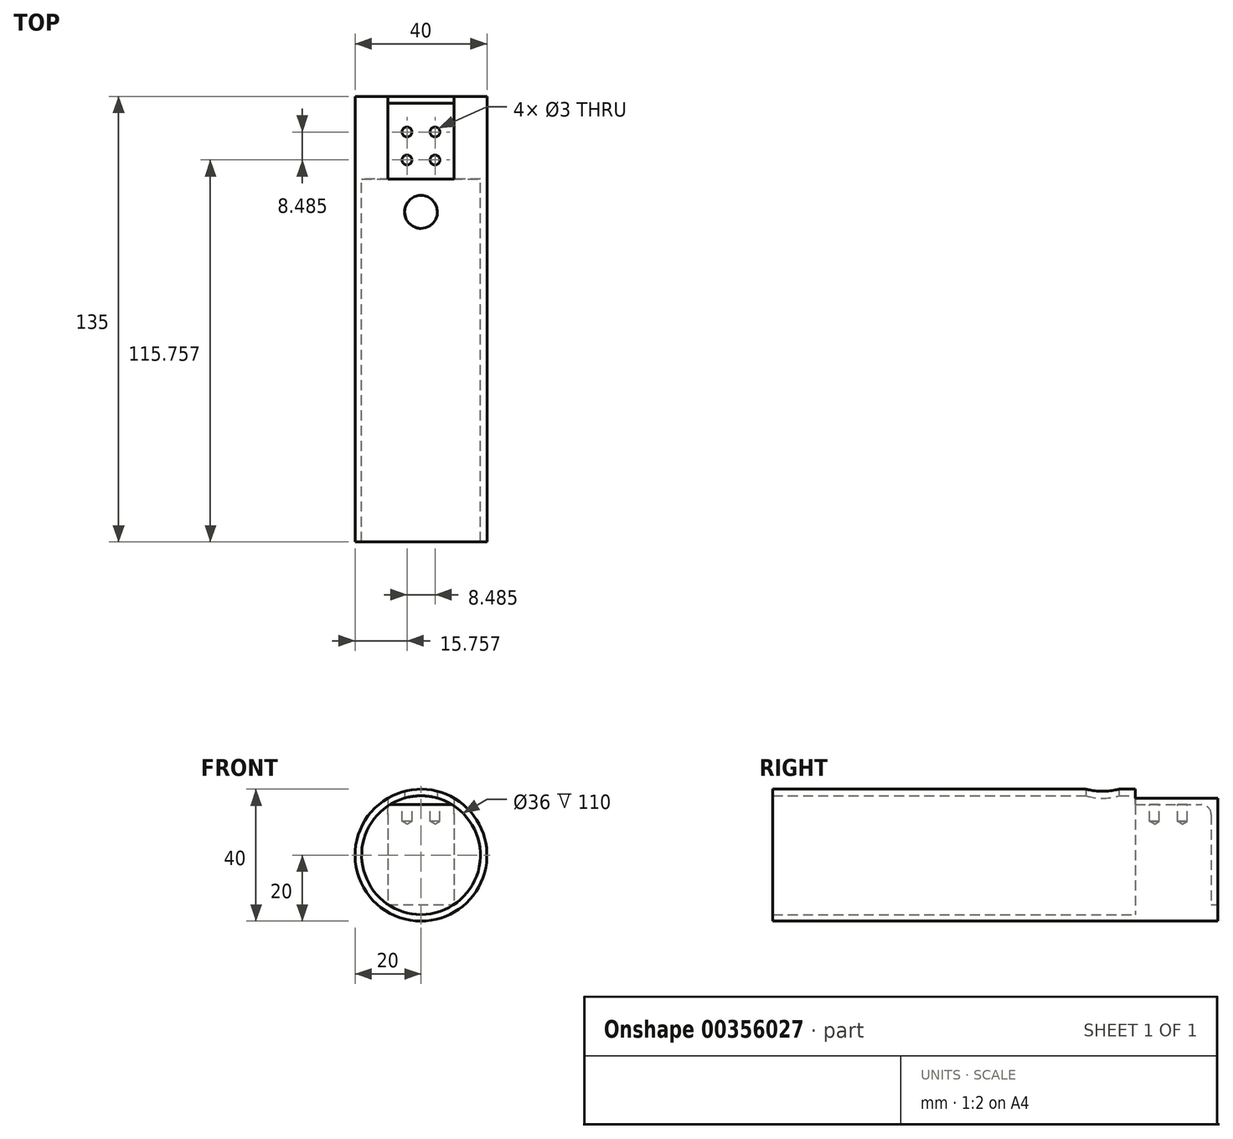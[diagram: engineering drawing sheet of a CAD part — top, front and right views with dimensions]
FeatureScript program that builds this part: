
annotation { "Feature Type Name" : "Feature", "Feature Type Description" : "" }
export const myFeature = defineFeature(function(context is Context, id is Id, definition is map)
    precondition{}
    {
        {
            var Q0;
            Q0=qCreatedBy(makeId("Front.planeOp"),FACE);
            var sketch = newSketch(context, id + "F0", { "sketchPlane" : qUnion([Q0])});
            skCircle(sketch, "E0", {"center": v(0, 0) * mm, "radius": 13.5 * mm});
            skCircle(sketch, "E1", {"center": v(0, 0) * mm, "radius": 20 * mm});
            skLineSegment(sketch, "E2.top", {"start": v(10, 15.32) * mm, "end": v(-10, 15.32) * mm});
            skLineSegment(sketch, "E2.left", {"start": v(10, 17.32) * mm, "end": v(10, 15.32) * mm});
            skLineSegment(sketch, "E2.right", {"start": v(-10, 17.32) * mm, "end": v(-10, 15.32) * mm});
            skPoint(sketch, "E3", {"position": v(10, 17.32) * mm});
            skCircle(sketch, "E4", {"center": v(0, 0) * mm, "radius": 18 * mm});
            skSolve(sketch);
        }
        {
            var Q0;
            {var subQ0=sQuery(id+"F0.wireOp",EDGE,"E2.left");Q0=makeQuery(id+"F0.imprint","IMPRINT",FACE,{"disambiguationData":[TD([[makeQuery(id+"F0.imprint","IMPRINT",EDGE,{"derivedFrom":subQ0}),1.0]])]});}
            extrude(context, id + "F1", {"entities" : qUnion([Q0]), "depth" : 135 * mm});
        }
        {
            var Q0;
            Q0=makeQuery(id+"F0.imprint","IMPRINT",FACE,{"disambiguationData":[TD([[makeQuery(id+"F0.imprint","IMPRINT",EDGE,{"derivedFrom":sQuery(id+"F0.wireOp",EDGE,"E2.top")}),-1.0]])]});
            extrude(context, id + "F2", {"entities" : qUnion([Q0]), "operationType" : NewBodyOperationType.ADD, "depth" : 135 * mm, "hasSecondDirection" : true, "secondDirectionOppositeDirection" : true, "secondDirectionDepth" : -25 * mm});
        }
        {
            var Q0;
            Q0=makeQuery(id+"F0.imprint","IMPRINT",FACE,{"disambiguationData":[TD([[makeQuery(id+"F0.imprint","IMPRINT",EDGE,{"derivedFrom":sQuery(id+"F0.wireOp",EDGE,"E0")}),1.0]])]});
            var Q1;
            Q1=makeQuery(id+"F0.imprint","IMPRINT",FACE,{"disambiguationData":[TD([[makeQuery(id+"F0.imprint","IMPRINT",EDGE,{"derivedFrom":sQuery(id+"F0.wireOp",EDGE,"E0")}),-1.0]])]});
            extrude(context, id + "F3", {"entities" : qUnion([Q0, Q1]), "operationType" : NewBodyOperationType.ADD, "depth" : 25 * mm});
        }
        {
            var Q0;
            Q0=qCreatedBy(makeId("Front.planeOp"),FACE);
            var sketch = newSketch(context, id + "F4", { "sketchPlane" : qUnion([Q0])});
            skLineSegment(sketch, "E5.bottom", {"start": v(-10, 21.25) * mm, "end": v(10, 21.25) * mm});
            skLineSegment(sketch, "E5.top", {"start": v(-10, -15) * mm, "end": v(10, -15) * mm});
            skLineSegment(sketch, "E5.left", {"start": v(-10, 21.25) * mm, "end": v(-10, -15) * mm});
            skLineSegment(sketch, "E5.right", {"start": v(10, 21.25) * mm, "end": v(10, -15) * mm});
            skSolve(sketch);
        }
        {
            var Q0;
            Q0 = qSketchRegion(id + "F4", true);
            extrude(context, id + "F5", {"entities" : qUnion([Q0]), "operationType" : NewBodyOperationType.REMOVE, "oppositeDirection" : true, "depth" : -2 * mm});
        }
        {
            var Q0;
            {var subQ0=sQuery(id+"F0.wireOp",EDGE,"E2.top");Q0=makeQuery(id+"F3.boolean.opBoolean","MERGE",FACE,{"derivedFrom":[makeQuery(id+"F1.opExtrude","SWEPT_FACE",FACE,{"disambiguationData":[OSD([subQ0]),TDD([makeQuery(id+"F0.imprint","IMPRINT",EDGE,{"disambiguationData":[TD([[makeQuery(id+"F0.imprint","INTERSECT",VERTEX,{"derivedFrom":[subQ0,sQuery(id+"F0.wireOp",EDGE,"E2.left")]}),-1.0]])],"derivedFrom":subQ0})])]}),makeQuery(id+"F1.opExtrude","SWEPT_FACE",FACE,{"disambiguationData":[OSD([subQ0]),TDD([makeQuery(id+"F0.imprint","IMPRINT",EDGE,{"disambiguationData":[TD([[makeQuery(id+"F0.imprint","INTERSECT",VERTEX,{"derivedFrom":[subQ0,sQuery(id+"F0.wireOp",EDGE,"E2.right")]}),1.0]])],"derivedFrom":subQ0})])]}),makeQuery(id+"F3.opExtrude","SWEPT_FACE",FACE,{"disambiguationData":[OSD([subQ0])]})]});}
            var sketch = newSketch(context, id + "F6", { "sketchPlane" : qUnion([Q0])});
            skPoint(sketch, "E6", {"position": v(0, -15) * mm});
            skPoint(sketch, "E7", {"position": v(0, -9) * mm});
            skPoint(sketch, "E8.1.0", {"position": v(-4.24, -10.76) * mm});
            skPoint(sketch, "E8.3.0", {"position": v(-4.24, -19.24) * mm});
            skPoint(sketch, "E8.5.0", {"position": v(4.24, -19.24) * mm});
            skPoint(sketch, "E8.7.0", {"position": v(4.24, -10.76) * mm});
            skSolve(sketch);
        }
        {
            var Q0;
            Q0=sQuery(id+"F6.wireOp",VERTEX,"E8.7.0");
            var Q1;
            Q1=sQuery(id+"F6.wireOp",VERTEX,"E8.1.0");
            var Q2;
            Q2=sQuery(id+"F6.wireOp",VERTEX,"E8.3.0");
            var Q3;
            Q3=sQuery(id+"F6.wireOp",VERTEX,"E8.5.0");
            var Q4;
            Q4=makeQuery(id+"F1.opExtrude","SWEPT_BODY",BODY,{"disambiguationData":[OSD([sQuery(id+"F0.wireOp",EDGE,"E1"),sQuery(id+"F0.wireOp",EDGE,"E2.top"),sQuery(id+"F0.wireOp",EDGE,"E2.left"),sQuery(id+"F0.wireOp",EDGE,"E2.right"),sQuery(id+"F0.wireOp",EDGE,"E4")])]});
            hole(context, id + "F7", {"style" : HoleStyle.SIMPLE, "endStyle" : HoleEndStyle.BLIND, "holeDiameter" : 3 * mm, "holeDepth" : 5 * mm, "tappedDepth" : 4 * mm, "tapClearance" : 3, "locations" : qUnion([Q0, Q1, Q2, Q3]), "scope" : qUnion([Q4])});
        }
        {
            var Q0;
            Q0=qCreatedBy(makeId("Top.planeOp"),FACE);
            var sketch = newSketch(context, id + "F8", { "sketchPlane" : qUnion([Q0])});
            skPoint(sketch, "E9", {"position": v(0, -35) * mm});
            skSolve(sketch);
        }
        {
            var Q0;
            Q0=sQuery(id+"F8.wireOp",VERTEX,"E9");
            var Q1;
            Q1=makeQuery(id+"F1.opExtrude","SWEPT_BODY",BODY,{"disambiguationData":[OSD([sQuery(id+"F0.wireOp",EDGE,"E1"),sQuery(id+"F0.wireOp",EDGE,"E2.top"),sQuery(id+"F0.wireOp",EDGE,"E2.left"),sQuery(id+"F0.wireOp",EDGE,"E2.right"),sQuery(id+"F0.wireOp",EDGE,"E4")])]});
            hole(context, id + "F9", {"style" : HoleStyle.SIMPLE, "endStyle" : HoleEndStyle.THROUGH, "oppositeDirection" : true, "holeDiameter" : 10 * mm, "tappedDepth" : 4 * mm, "tapClearance" : 3, "locations" : qUnion([Q0]), "scope" : qUnion([Q1])});
        }
        {
            var Q0;
            {var subQ0=sQuery(id+"F0.wireOp",EDGE,"E2.top");Q0=makeQuery(id+"F5.boolean.opBoolean","INTERSECT",EDGE,{"derivedFrom":[makeQuery(id+"F3.boolean.opBoolean","MERGE",FACE,{"derivedFrom":[makeQuery(id+"F1.opExtrude","SWEPT_FACE",FACE,{"disambiguationData":[OSD([subQ0]),TDD([makeQuery(id+"F0.imprint","IMPRINT",EDGE,{"disambiguationData":[TD([[makeQuery(id+"F0.imprint","INTERSECT",VERTEX,{"derivedFrom":[subQ0,sQuery(id+"F0.wireOp",EDGE,"E2.left")]}),-1.0]])],"derivedFrom":subQ0})])]}),makeQuery(id+"F1.opExtrude","SWEPT_FACE",FACE,{"disambiguationData":[OSD([subQ0]),TDD([makeQuery(id+"F0.imprint","IMPRINT",EDGE,{"disambiguationData":[TD([[makeQuery(id+"F0.imprint","INTERSECT",VERTEX,{"derivedFrom":[subQ0,sQuery(id+"F0.wireOp",EDGE,"E2.right")]}),1.0]])],"derivedFrom":subQ0})])]}),makeQuery(id+"F3.opExtrude","SWEPT_FACE",FACE,{"disambiguationData":[OSD([subQ0])]})]}),makeQuery(id+"F5.opExtrude","CAP_FACE",FACE,{"disambiguationData":[OSD([sQuery(id+"F4.wireOp",EDGE,"E5.bottom"),sQuery(id+"F4.wireOp",EDGE,"E5.top"),sQuery(id+"F4.wireOp",EDGE,"E5.left"),sQuery(id+"F4.wireOp",EDGE,"E5.right")])],"isStart":false})]});}
            fillet(context, id + "F10", {"entities" : qUnion([Q0]), "radius" : 3 * mm, "tangentPropagation" : true, "allowEdgeOverflow" : false});
        }
    });
